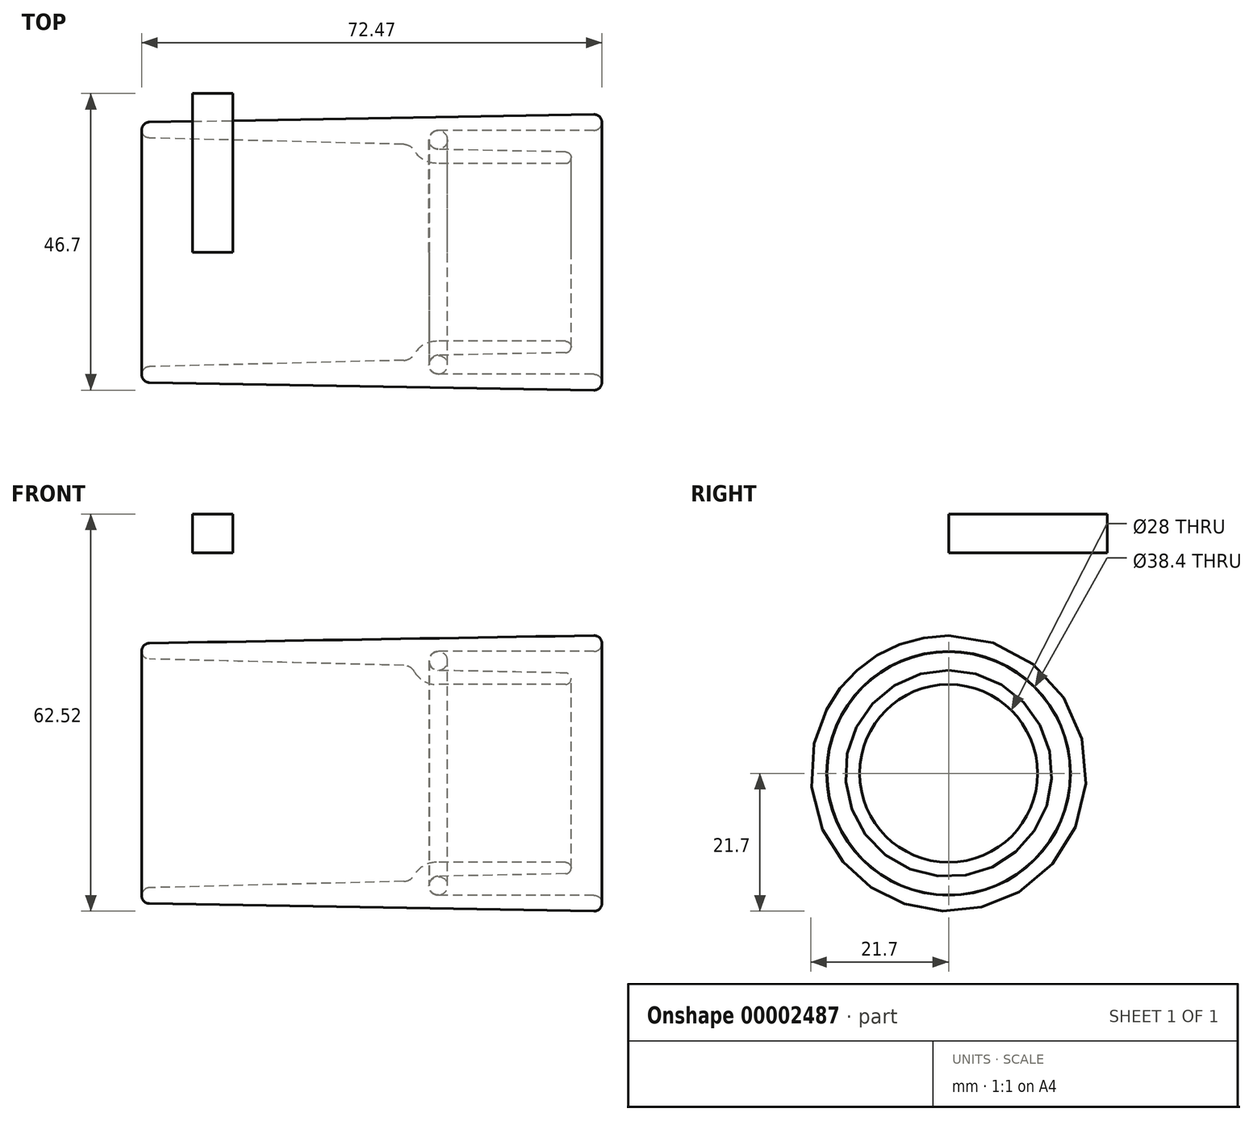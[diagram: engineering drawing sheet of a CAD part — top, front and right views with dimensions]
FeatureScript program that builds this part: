
annotation { "Feature Type Name" : "Feature", "Feature Type Description" : "" }
export const myFeature = defineFeature(function(context is Context, id is Id, definition is map)
    precondition{}
    {
        {
            var Q0;
            Q0=qCreatedBy(makeId("Front.planeOp"),FACE);
            var sketch = newSketch(context, id + "F0", { "sketchPlane" : qUnion([Q0])});
            skLineSegment(sketch, "E0", {"start": v(-53.32, 0) * mm, "end": v(61.4, 0) * mm, "construction": true});
            skLineSegment(sketch, "E1", {"start": v(30, 19.2) * mm, "end": v(5.5, 19.2) * mm});
            skLineSegment(sketch, "E2", {"start": v(5.47, 16.2) * mm, "end": v(25.52, 15.8) * mm});
            skLineSegment(sketch, "E3", {"start": v(25.5, 14) * mm, "end": v(5.2, 14) * mm});
            skLineSegment(sketch, "E4", {"start": v(0.05, 17) * mm, "end": v(-40, 18) * mm});
            skLineSegment(sketch, "E5", {"start": v(29.98, 21.7) * mm, "end": v(-40, 20.5) * mm});
            skArc(sketch, "E6", {"start": v(5.47, 16.2) * mm, "mid": v(4, 17.71) * mm, "end": v(5.5, 19.2) * mm});
            skCircle(sketch, "E7", {"center": v(5.5, 17.7) * mm, "radius": 1.45 * mm});
            skPoint(sketch, "E8.visualSharp", {"position": v(0, 17) * mm});
            skArc(sketch, "E8.filletArc", {"start": v(1.73, 16) * mm, "mid": v(1.02, 16.72) * mm, "end": v(0.05, 17) * mm});
            skPoint(sketch, "E9.visualSharp", {"position": v(0, 14) * mm});
            skArc(sketch, "E9.filletArc", {"start": v(1.73, 16) * mm, "mid": v(3.2, 14.54) * mm, "end": v(5.2, 14) * mm});
            skArc(sketch, "E10", {"start": v(25.5, 14) * mm, "mid": v(26.4, 14.9) * mm, "end": v(25.52, 15.8) * mm});
            skArc(sketch, "E11", {"start": v(-40, 20.5) * mm, "mid": v(-41.22, 19.25) * mm, "end": v(-40, 18) * mm});
            skArc(sketch, "E12", {"start": v(29.98, 21.7) * mm, "mid": v(31.25, 20.46) * mm, "end": v(30, 19.2) * mm});
            skSolve(sketch);
        }
        {
            var Q0;
            Q0=makeQuery(id+"F0.imprint","IMPRINT",FACE,{"disambiguationData":[TD([[makeQuery(id+"F0.imprint","IMPRINT",EDGE,{"derivedFrom":sQuery(id+"F0.wireOp",EDGE,"E1")}),-1.0]])]});
            var Q1;
            Q1=makeQuery(id+"F0.imprint","IMPRINT",FACE,{"disambiguationData":[TD([[makeQuery(id+"F0.imprint","IMPRINT",EDGE,{"derivedFrom":sQuery(id+"F0.wireOp",EDGE,"E7")}),1.0]])]});
            var Q2;
            Q2=sQuery(id+"F0.wireOp",EDGE,"E0");
            revolve(context, id + "F1", {"entities" : qUnion([Q0, Q1]), "axis" : qUnion([Q2]), "revolveType" : RevolveType.FULL});
        }
        {
            var Q0;
            Q0=qCreatedBy(makeId("Front.planeOp"),FACE);
            var sketch = newSketch(context, id + "F2", { "sketchPlane" : qUnion([Q0])});
            skLineSegment(sketch, "E13.bottom", {"start": v(-33.22, 40.82) * mm, "end": v(-26.84, 40.82) * mm});
            skLineSegment(sketch, "E13.top", {"start": v(-33.22, 34.69) * mm, "end": v(-26.84, 34.69) * mm});
            skLineSegment(sketch, "E13.left", {"start": v(-33.22, 40.82) * mm, "end": v(-33.22, 34.69) * mm});
            skLineSegment(sketch, "E13.right", {"start": v(-26.84, 40.82) * mm, "end": v(-26.84, 34.69) * mm});
            skSolve(sketch);
        }
        {
            var Q0;
            Q0=makeQuery(id+"F2.imprint","IMPRINT",FACE,{"disambiguationData":[TD([[makeQuery(id+"F2.imprint","IMPRINT",EDGE,{"derivedFrom":sQuery(id+"F2.wireOp",EDGE,"E13.bottom")}),-1.0]])]});
            extrude(context, id + "F3", {"entities" : qUnion([Q0]), "oppositeDirection" : true, "depth" : 25 * mm});
        }
    });
